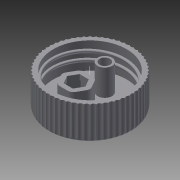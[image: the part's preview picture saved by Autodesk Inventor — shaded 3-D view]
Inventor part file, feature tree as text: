
AUTODESK INVENTOR PART (.ipt)
format: ipt  version: 2015 SP1 (Build 190203100, 203)  size: 589,312 bytes
history: native  units: mm
features: sketch x9, extrude x8, fillet x4, other x2, projected_geometry x2, pattern_circular x1
ambient origin geometry x8: Origin, YZ Plane, XZ Plane, XY Plane, X Axis, Y Axis, Z Axis, Center Point
bodies: Body1 (feature_tree), Body2 (feature_tree), Body3 (feature_tree), Body4 (feature_tree), Body5 (feature_tree), Body6 (feature_tree)
feature tree (26):
  other  "Sólido1"
  extrude  "Extrusión1"  Depth=32.0mm
  extrude  "Extrusión2"  Depth=3.0mm
  other  "Bobina1"
  extrude  "Extrusión3"  Depth=10.0mm TaperAngle=0.0deg
  extrude  "Extrusión4"  Depth=2.0mm TaperAngle=0.0deg
  extrude  "Extrusión5"  Depth=2.0mm
  fillet  "Empalme1"  Radius=1.3mm
  fillet  "Empalme2"  Radius=1.5mm
  extrude  "Extrusión6"  Depth=0.35mm
  pattern_circular  "Patrón circular1"  Count=60 Angle=360.0deg
  extrude  "Extrusión7"  Depth=2.0mm
  extrude  "Extrusión8"  Depth=10.0mm TaperAngle=0.0deg
  fillet  "Empalme3"  Radius=4.0mm
  fillet  "Empalme4"  Radius=12.0mm
  sketch  "Boceto1"  dims[d0=28.0mm d1=32.0mm]
  sketch  "Boceto2"  dims[d2=3.0mm d3=0.0mm d4=28.0mm]
  sketch  "Boceto3"  dims[d5=10.0mm d6=0.0mm]
  projected_geometry  "Contorno proyectado1"
  sketch  "Boceto4"  dims[d11=3.0mm d12=10.0mm d13=14.0mm d14=0.0mm d15=90.0deg d16=90.0deg d17=0.0mm d18=0.0mm d20=10.0mm d21=0.0mm]
  sketch  "Boceto5"  dims[d22=7.0mm d23=0.0mm d24=2.0mm d25=0.0mm]
  sketch  "Boceto6"  dims[d26=2.0mm d28=2.0mm d29=1.3mm d30=1.5mm]
  sketch  "Boceto7"  dims[d31=90.0deg d32=0.35mm]
  sketch  "Boceto8"  dims[d34=7.0mm]
  sketch  "Boceto9"  dims[d35=177.0mm d36=0.0mm d37=600.0mm d38=360.0deg d40=5.5mm d41=10.0mm d42=0.0mm d43=4.0mm d44=12.0mm d45=0.0mm d46=2.0mm d48=2.0mm d49=9.36mm]
  projected_geometry  "Contorno proyectado4"
